# Revit family: ProVista™ Sashless Double Hung Window- SS SF FS
name_source: partatom
category: Windows
units: mm (PartAtom-declared; Revit-internal decimal feet)

## family parameters
Always vertical = Yes
Cut with Voids When Loaded = No
Host = Wall
OmniClass Number = 23.30.20.00
OmniClass Title = Windows
Room Calculation Point = No
Shared = No

## types (1)
- SS
    Analytic Construction = <None>
    Default Sill Height = 900 mm
    Define Thermal Properties by = Schematic Type
    FRAME THICKNESS = 101.6 mm  [stored 0.333333 ft]
    Height = 0 mm  [stored 0 ft]
    Manufacturer = ALSPEC
    Model = ProVista™ Sashless Double Hung Window- SS SF FS
    Rough Height = 0 mm  [stored 0 ft]
    Rough Width = 0 mm  [stored 0 ft]
    SINGLE GLAZED THICKNESS = 6 mm  [stored 0.019685 ft]
    URL = https://www.alspec.com.au
    Wall Closure = By host
    Width = 0 mm  [stored 0 ft]
    X = 100 mm  [stored 0.328084 ft]
    YEAR = 2022

note: [stored X ft] marks values corroborated as IEEE doubles in the binary element streams (Revit-internal decimal feet)

## geometry (parser evidence)
native form markers: Sweep x12
no freeform markers — native parametric forms only
